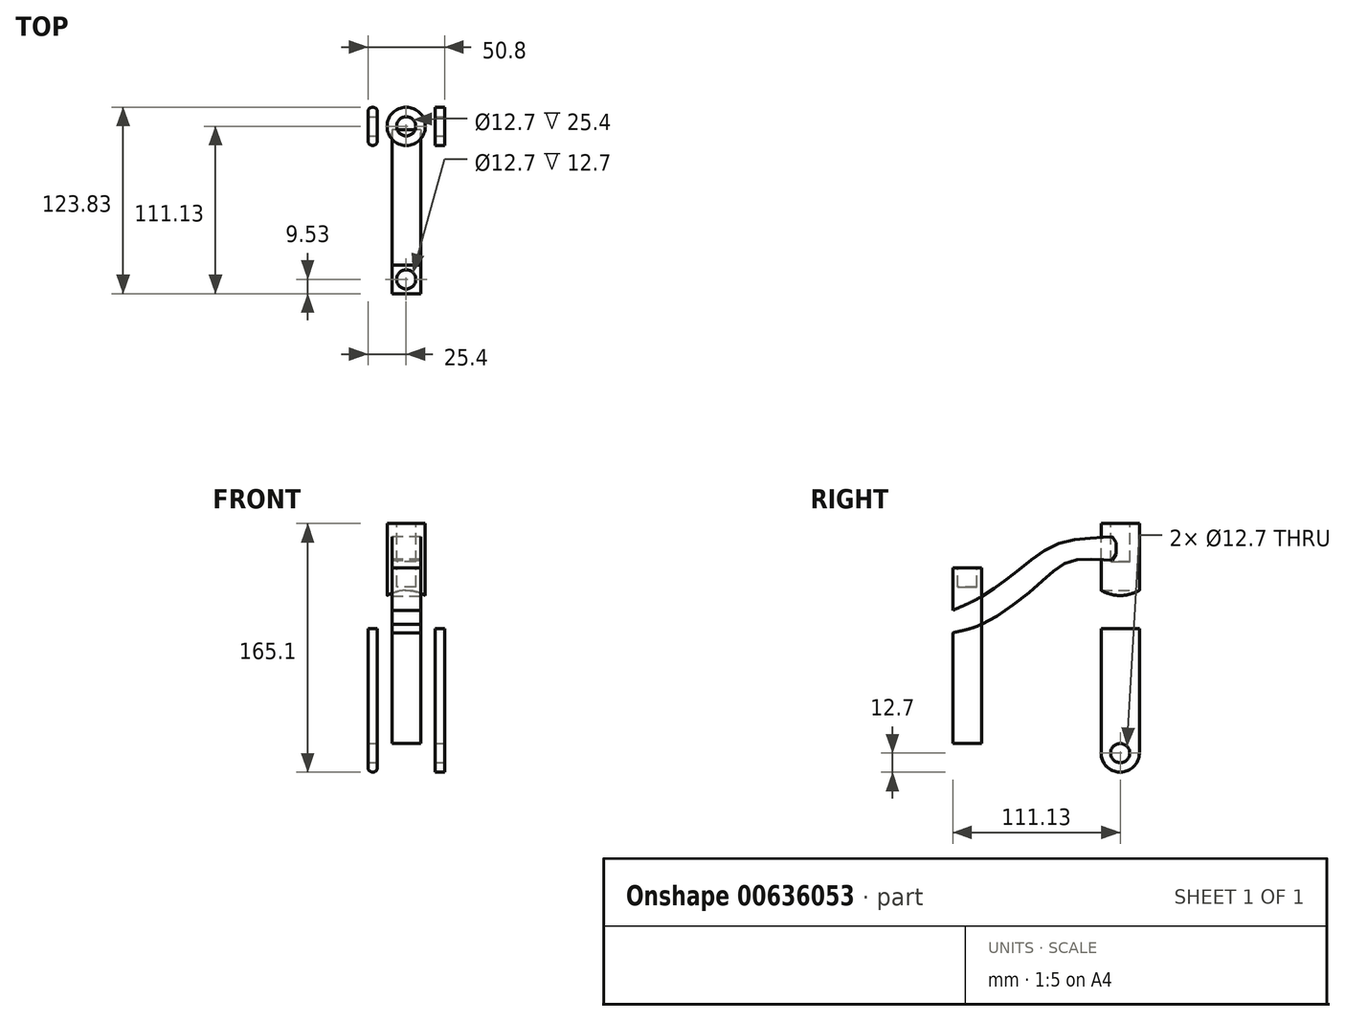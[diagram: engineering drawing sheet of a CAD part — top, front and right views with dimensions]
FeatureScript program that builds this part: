
annotation { "Feature Type Name" : "Feature", "Feature Type Description" : "" }
export const myFeature = defineFeature(function(context is Context, id is Id, definition is map)
    precondition{}
    {
        {
            var Q0;
            Q0=qCreatedBy(makeId("Front.planeOp"),FACE);
            var sketch = newSketch(context, id + "F0", { "sketchPlane" : qUnion([Q0])});
            skLineSegment(sketch, "E0", {"start": v(-133.38, 0) * mm, "end": v(142.58, 0) * mm});
            skLineSegment(sketch, "E1.0", {"start": v(-133.38, 12.7) * mm, "end": v(142.58, 12.7) * mm});
            skLineSegment(sketch, "E2.0", {"start": v(-133.38, 19.05) * mm, "end": v(142.58, 19.05) * mm});
            skLineSegment(sketch, "E3.0", {"start": v(-133.38, 88.9) * mm, "end": v(142.58, 88.9) * mm});
            skLineSegment(sketch, "E4", {"start": v(0, 134.77) * mm, "end": v(0, -117.55) * mm});
            skLineSegment(sketch, "E5.0", {"start": v(-19.05, 76.2) * mm, "end": v(-19.05, -19.05) * mm});
            skLineSegment(sketch, "E6.0", {"start": v(19.05, 76.2) * mm, "end": v(19.05, -19.05) * mm});
            skLineSegment(sketch, "E7.0", {"start": v(-133.38, 76.2) * mm, "end": v(142.58, 76.2) * mm});
            skArc(sketch, "E8", {"start": v(19.05, 76.2) * mm, "mid": v(0, 95.25) * mm, "end": v(-19.05, 76.2) * mm});
            skLineSegment(sketch, "E9.0", {"start": v(-6.35, 146.05) * mm, "end": v(-6.35, 100.8) * mm});
            skLineSegment(sketch, "E10.0", {"start": v(6.35, 146.05) * mm, "end": v(6.35, 100.8) * mm});
            skLineSegment(sketch, "E11.0", {"start": v(-12.7, 146.05) * mm, "end": v(12.7, 146.05) * mm});
            skLineSegment(sketch, "E12.0", {"start": v(-12.7, 146.05) * mm, "end": v(-12.7, 98.2) * mm});
            skLineSegment(sketch, "E12.2", {"start": v(12.7, 146.05) * mm, "end": v(12.7, 98.2) * mm});
            skLineSegment(sketch, "E13.0", {"start": v(25.4, 76.2) * mm, "end": v(25.4, -19.05) * mm});
            skArc(sketch, "E13.1", {"start": v(25.4, 76.2) * mm, "mid": v(0, 101.6) * mm, "end": v(-25.4, 76.2) * mm});
            skLineSegment(sketch, "E13.2", {"start": v(-25.4, 76.2) * mm, "end": v(-25.4, -19.05) * mm});
            skLineSegment(sketch, "E14.0", {"start": v(-25.4, -19.05) * mm, "end": v(-19.05, -19.05) * mm});
            skLineSegment(sketch, "E15.trimOffspring", {"start": v(19.05, -19.05) * mm, "end": v(25.4, -19.05) * mm});
            skLineSegment(sketch, "E16.trimOffspring", {"start": v(6.35, 94.16) * mm, "end": v(6.35, -117.55) * mm});
            skLineSegment(sketch, "E17.trimOffspring", {"start": v(-6.35, 94.16) * mm, "end": v(-6.35, -117.55) * mm});
            skSolve(sketch);
        }
        {
            var Q0;
            {var subQ4=sQuery(id+"F0.wireOp",EDGE,"E13.1");var subQ6=sQuery(id+"F0.wireOp",EDGE,"E3.0");var subQ8=makeQuery(id+"F0.imprint","INTERSECT",VERTEX,{"disambiguationData":[OD(0.0)],"derivedFrom":[subQ6,subQ4]});Q0=makeQuery(id+"F0.imprint","IMPRINT",FACE,{"disambiguationData":[TD([[makeQuery(id+"F0.imprint","IMPRINT",EDGE,{"disambiguationData":[TD([[subQ8,-1.0]])],"derivedFrom":subQ6}),1.0]])]});}
            var Q1;
            {var subQ0=sQuery(id+"F0.wireOp",EDGE,"E13.1");var subQ1=sQuery(id+"F0.wireOp",EDGE,"E3.0");var subQ2=makeQuery(id+"F0.imprint","INTERSECT",VERTEX,{"disambiguationData":[OD(0.0)],"derivedFrom":[subQ1,subQ0]});Q1=makeQuery(id+"F0.imprint","IMPRINT",FACE,{"disambiguationData":[TD([[makeQuery(id+"F0.imprint","IMPRINT",EDGE,{"disambiguationData":[TD([[subQ2,-1.0]])],"derivedFrom":subQ1}),-1.0]])]});}
            var Q2;
            {var subQ4=sQuery(id+"F0.wireOp",EDGE,"E13.1");var subQ6=sQuery(id+"F0.wireOp",EDGE,"E3.0");var subQ8=makeQuery(id+"F0.imprint","INTERSECT",VERTEX,{"disambiguationData":[OD(1.0)],"derivedFrom":[subQ6,subQ4]});Q2=makeQuery(id+"F0.imprint","IMPRINT",FACE,{"disambiguationData":[TD([[makeQuery(id+"F0.imprint","IMPRINT",EDGE,{"disambiguationData":[TD([[subQ8,1.0]])],"derivedFrom":subQ6}),1.0]])]});}
            var Q3;
            {var subQ0=sQuery(id+"F0.wireOp",EDGE,"E13.1");var subQ1=sQuery(id+"F0.wireOp",EDGE,"E3.0");var subQ2=makeQuery(id+"F0.imprint","INTERSECT",VERTEX,{"disambiguationData":[OD(1.0)],"derivedFrom":[subQ1,subQ0]});Q3=makeQuery(id+"F0.imprint","IMPRINT",FACE,{"disambiguationData":[TD([[makeQuery(id+"F0.imprint","IMPRINT",EDGE,{"disambiguationData":[TD([[subQ2,1.0]])],"derivedFrom":subQ1}),-1.0]])]});}
            var Q4;
            {var subQ0=sQuery(id+"F0.wireOp",EDGE,"E13.0");var subQ1=sQuery(id+"F0.wireOp",EDGE,"E2.0");var subQ2=makeQuery(id+"F0.imprint","INTERSECT",VERTEX,{"derivedFrom":[subQ1,subQ0]});Q4=makeQuery(id+"F0.imprint","IMPRINT",FACE,{"disambiguationData":[TD([[makeQuery(id+"F0.imprint","IMPRINT",EDGE,{"disambiguationData":[TD([[subQ2,1.0]])],"derivedFrom":subQ1}),1.0]])]});}
            var Q5;
            {var subQ0=sQuery(id+"F0.wireOp",EDGE,"E13.0");var subQ1=sQuery(id+"F0.wireOp",EDGE,"E1.0");var subQ2=makeQuery(id+"F0.imprint","INTERSECT",VERTEX,{"derivedFrom":[subQ1,subQ0]});Q5=makeQuery(id+"F0.imprint","IMPRINT",FACE,{"disambiguationData":[TD([[makeQuery(id+"F0.imprint","IMPRINT",EDGE,{"disambiguationData":[TD([[subQ2,1.0]])],"derivedFrom":subQ1}),1.0]])]});}
            var Q6;
            {var subQ0=sQuery(id+"F0.wireOp",EDGE,"E13.0");var subQ1=sQuery(id+"F0.wireOp",EDGE,"E0");var subQ2=makeQuery(id+"F0.imprint","INTERSECT",VERTEX,{"derivedFrom":[subQ1,subQ0]});Q6=makeQuery(id+"F0.imprint","IMPRINT",FACE,{"disambiguationData":[TD([[makeQuery(id+"F0.imprint","IMPRINT",EDGE,{"disambiguationData":[TD([[subQ2,1.0]])],"derivedFrom":subQ1}),1.0]])]});}
            var Q7;
            {var subQ5=sQuery(id+"F0.wireOp",EDGE,"E15.trimOffspring");Q7=makeQuery(id+"F0.imprint","IMPRINT",FACE,{"disambiguationData":[TD([[makeQuery(id+"F0.imprint","IMPRINT",EDGE,{"derivedFrom":subQ5}),1.0]])]});}
            var Q8;
            {var subQ5=sQuery(id+"F0.wireOp",EDGE,"E14.0");Q8=makeQuery(id+"F0.imprint","IMPRINT",FACE,{"disambiguationData":[TD([[makeQuery(id+"F0.imprint","IMPRINT",EDGE,{"derivedFrom":subQ5}),1.0]])]});}
            var Q9;
            {var subQ0=sQuery(id+"F0.wireOp",EDGE,"E13.2");var subQ1=sQuery(id+"F0.wireOp",EDGE,"E0");var subQ2=makeQuery(id+"F0.imprint","INTERSECT",VERTEX,{"derivedFrom":[subQ1,subQ0]});Q9=makeQuery(id+"F0.imprint","IMPRINT",FACE,{"disambiguationData":[TD([[makeQuery(id+"F0.imprint","IMPRINT",EDGE,{"disambiguationData":[TD([[subQ2,-1.0]])],"derivedFrom":subQ1}),1.0]])]});}
            var Q10;
            {var subQ0=sQuery(id+"F0.wireOp",EDGE,"E13.2");var subQ1=sQuery(id+"F0.wireOp",EDGE,"E1.0");var subQ2=makeQuery(id+"F0.imprint","INTERSECT",VERTEX,{"derivedFrom":[subQ1,subQ0]});Q10=makeQuery(id+"F0.imprint","IMPRINT",FACE,{"disambiguationData":[TD([[makeQuery(id+"F0.imprint","IMPRINT",EDGE,{"disambiguationData":[TD([[subQ2,-1.0]])],"derivedFrom":subQ1}),1.0]])]});}
            var Q11;
            {var subQ0=sQuery(id+"F0.wireOp",EDGE,"E13.2");var subQ1=sQuery(id+"F0.wireOp",EDGE,"E2.0");var subQ2=makeQuery(id+"F0.imprint","INTERSECT",VERTEX,{"derivedFrom":[subQ1,subQ0]});Q11=makeQuery(id+"F0.imprint","IMPRINT",FACE,{"disambiguationData":[TD([[makeQuery(id+"F0.imprint","IMPRINT",EDGE,{"disambiguationData":[TD([[subQ2,-1.0]])],"derivedFrom":subQ1}),1.0]])]});}
            extrude(context, id + "F1", {"entities" : qUnion([Q0, Q1, Q2, Q3, Q4, Q5, Q6, Q7, Q8, Q9, Q10, Q11]), "endBound" : BoundingType.SYMMETRIC, "oppositeDirection" : true, "depth" : 25.4 * mm, "offsetDistance" : 25.4 * mm});
        }
        {
            var Q0;
            Q0=makeQuery(id+"F1.opExtrude","CAP_EDGE",EDGE,{"disambiguationData":[OSD([sQuery(id+"F0.wireOp",EDGE,"E14.0")])],"isStart":true});
            var Q1;
            Q1=makeQuery(id+"F1.opExtrude","CAP_EDGE",EDGE,{"disambiguationData":[OSD([sQuery(id+"F0.wireOp",EDGE,"E15.trimOffspring")])],"isStart":true});
            var Q2;
            Q2=makeQuery(id+"F1.opExtrude","CAP_EDGE",EDGE,{"disambiguationData":[OSD([sQuery(id+"F0.wireOp",EDGE,"E15.trimOffspring")])],"isStart":false});
            var Q3;
            Q3=makeQuery(id+"F1.opExtrude","CAP_EDGE",EDGE,{"disambiguationData":[OSD([sQuery(id+"F0.wireOp",EDGE,"E14.0")])],"isStart":false});
            fillet(context, id + "F2", {"entities" : qUnion([Q0, Q1, Q2, Q3]), "radius" : 12.7 * mm, "tangentPropagation" : true, "allowEdgeOverflow" : false});
        }
        {
            var Q0;
            Q0=makeQuery(id+"F1.opExtrude","SWEPT_FACE",FACE,{"disambiguationData":[OSD([sQuery(id+"F0.wireOp",EDGE,"E13.2")])]});
            var sketch = newSketch(context, id + "F3", { "sketchPlane" : qUnion([Q0])});
            skCircle(sketch, "E18", {"center": v(0, -6.35) * mm, "radius": 6.35 * mm});
            skSolve(sketch);
        }
        {
            var Q0;
            Q0=makeQuery(id+"F3.imprint","IMPRINT",FACE,{"disambiguationData":[TD([[makeQuery(id+"F3.imprint","IMPRINT",EDGE,{"derivedFrom":sQuery(id+"F3.wireOp",EDGE,"E18")}),1.0]])]});
            var Q1;
            Q1=makeQuery(id+"F1.opExtrude","SWEPT_FACE",FACE,{"disambiguationData":[OSD([sQuery(id+"F0.wireOp",EDGE,"E13.0")])]});
            extrude(context, id + "F4", {"entities" : qUnion([Q0]), "operationType" : NewBodyOperationType.REMOVE, "depth" : 25.4 * mm, "offsetDistance" : 25.4 * mm, "hasSecondDirection" : true, "secondDirectionBound" : SecondDirectionBoundingType.UP_TO_SURFACE, "secondDirectionOppositeDirection" : true, "secondDirectionDepth" : 25.4 * mm, "secondDirectionBoundEntityFace" : qUnion([Q1])});
        }
        {
            var Q0;
            {var subQ0=sQuery(id+"F0.wireOp",EDGE,"E9.0");Q0=makeQuery(id+"F0.imprint","IMPRINT",FACE,{"disambiguationData":[TD([[makeQuery(id+"F0.imprint","IMPRINT",EDGE,{"derivedFrom":subQ0}),-1.0]])]});}
            var Q1;
            {var subQ4=sQuery(id+"F0.wireOp",EDGE,"E9.0");Q1=makeQuery(id+"F0.imprint","IMPRINT",FACE,{"disambiguationData":[TD([[makeQuery(id+"F0.imprint","IMPRINT",EDGE,{"derivedFrom":subQ4}),1.0]])]});}
            var Q2;
            {var subQ0=sQuery(id+"F0.wireOp",EDGE,"E10.0");Q2=makeQuery(id+"F0.imprint","IMPRINT",FACE,{"disambiguationData":[TD([[makeQuery(id+"F0.imprint","IMPRINT",EDGE,{"derivedFrom":subQ0}),1.0]])]});}
            extrude(context, id + "F5", {"entities" : qUnion([Q0, Q1, Q2]), "endBound" : BoundingType.SYMMETRIC, "depth" : 25.4 * mm, "offsetDistance" : 25.4 * mm});
        }
        {
            var Q0;
            Q0=makeQuery(id+"F5.opExtrude","SWEPT_FACE",FACE,{"disambiguationData":[OSD([sQuery(id+"F0.wireOp",EDGE,"E11.0")])]});
            var sketch = newSketch(context, id + "F6", { "sketchPlane" : qUnion([Q0])});
            skCircle(sketch, "E19", {"center": v(0, 0) * mm, "radius": 6.35 * mm});
            skSolve(sketch);
        }
        {
            var Q0;
            Q0=makeQuery(id+"F6.imprint","IMPRINT",FACE,{"disambiguationData":[TD([[makeQuery(id+"F6.imprint","IMPRINT",EDGE,{"derivedFrom":sQuery(id+"F6.wireOp",EDGE,"E19")}),1.0]])]});
            extrude(context, id + "F7", {"entities" : qUnion([Q0]), "operationType" : NewBodyOperationType.REMOVE, "oppositeDirection" : true, "depth" : 25.4 * mm, "offsetDistance" : 25.4 * mm});
        }
        {
            var Q0;
            Q0=makeQuery(id+"F5.opExtrude","CAP_EDGE",EDGE,{"disambiguationData":[OSD([sQuery(id+"F0.wireOp",EDGE,"E12.0")])],"isStart":true});
            var Q1;
            Q1=makeQuery(id+"F5.opExtrude","CAP_EDGE",EDGE,{"disambiguationData":[OSD([sQuery(id+"F0.wireOp",EDGE,"E12.0")])],"isStart":false});
            var Q2;
            Q2=makeQuery(id+"F5.opExtrude","CAP_EDGE",EDGE,{"disambiguationData":[OSD([sQuery(id+"F0.wireOp",EDGE,"E12.2")])],"isStart":false});
            var Q3;
            Q3=makeQuery(id+"F5.opExtrude","CAP_EDGE",EDGE,{"disambiguationData":[OSD([sQuery(id+"F0.wireOp",EDGE,"E12.2")])],"isStart":true});
            fillet(context, id + "F8", {"entities" : qUnion([Q0, Q1, Q2, Q3]), "radius" : 12.7 * mm, "tangentPropagation" : true, "allowEdgeOverflow" : false});
        }
        {
            var Q0;
            Q0=makeQuery(id+"F1.opExtrude","CAP_EDGE",EDGE,{"disambiguationData":[OSD([sQuery(id+"F0.wireOp",EDGE,"E13.2")])],"isStart":true});
            var Q1;
            Q1=makeQuery(id+"F1.opExtrude","CAP_EDGE",EDGE,{"disambiguationData":[OSD([sQuery(id+"F0.wireOp",EDGE,"E5.0")])],"isStart":true});
            fillet(context, id + "F9", {"entities" : qUnion([Q0, Q1]), "radius" : 3.17 * mm, "tangentPropagation" : true, "allowEdgeOverflow" : false});
        }
        {
            var Q0;
            Q0=qCreatedBy(makeId("Right.planeOp"),FACE);
            var sketch = newSketch(context, id + "F10", { "sketchPlane" : qUnion([Q0])});
            skLineSegment(sketch, "E20", {"start": v(0, 167.43) * mm, "end": v(0, -72.36) * mm});
            skLineSegment(sketch, "E21.0", {"start": v(-101.6, 167.43) * mm, "end": v(-101.6, -72.36) * mm});
            skLineSegment(sketch, "E22.0", {"start": v(-203.2, 167.43) * mm, "end": v(-203.2, 97.58) * mm});
            skLineSegment(sketch, "E23", {"start": v(-101.6, 167.43) * mm, "end": v(-203.2, 167.43) * mm});
            skLineSegment(sketch, "E24.0", {"start": v(-92.08, 116.63) * mm, "end": v(-111.13, 116.63) * mm});
            skLineSegment(sketch, "E25.0", {"start": v(-92.07, 97.58) * mm, "end": v(-111.12, 97.58) * mm});
            skLineSegment(sketch, "E26", {"start": v(0, 0) * mm, "end": v(-203.2, 0) * mm});
            skLineSegment(sketch, "E27.0", {"start": v(0, -12.7) * mm, "end": v(-203.2, -12.7) * mm});
            skLineSegment(sketch, "E28.0", {"start": v(0, -19.05) * mm, "end": v(-203.2, -19.05) * mm});
            skCircle(sketch, "E29", {"center": v(-203.2, -6.35) * mm, "radius": 6.35 * mm});
            skCircle(sketch, "E30", {"center": v(-203.2, -6.35) * mm, "radius": 12.7 * mm});
            skLineSegment(sketch, "E31.0", {"start": v(-92.08, 116.63) * mm, "end": v(-92.07, -72.36) * mm});
            skLineSegment(sketch, "E32.0", {"start": v(-111.13, 116.63) * mm, "end": v(-111.12, -72.36) * mm});
            skFitSpline(sketch, "E33", {"points": [v(-10.52, 136.84) * mm, v(-39.13, 133.26) * mm, v(-67.1, 115.5) * mm, v(-92.07, 97.58) * mm, v(-118.86, 85.47) * mm, v(-159.5, 64.15) * mm, v(-211.86, 2.93) * mm, v(-211.9, -2.96) * mm, v(-194.22, -10.04) * mm, v(-190.5, -6.35) * mm, v(-186.18, 10.6) * mm, v(-156.28, 51.58) * mm, v(-116.42, 72.26) * mm, v(-92.07, 79.05) * mm, v(-53.74, 105.85) * mm, v(-33.35, 120.81) * mm, v(-10.16, 121.75) * mm, v(-3.8, 122.9) * mm, v(-3.57, 135.9) * mm, v(-10.52, 136.84) * mm]});
            skSolve(sketch);
        }
        {
            var Q0;
            {var subQ0=sQuery(id+"F10.wireOp",EDGE,"E33");var subQ1=sQuery(id+"F10.wireOp",EDGE,"E31.0");var subQ3=makeQuery(id+"F10.imprint","INTERSECT",VERTEX,{"derivedFrom":[subQ1,subQ0]});Q0=makeQuery(id+"F10.imprint","IMPRINT",FACE,{"disambiguationData":[TD([[makeQuery(id+"F10.imprint","IMPRINT",EDGE,{"disambiguationData":[TD([[subQ3,1.0]])],"derivedFrom":subQ1}),1.0]])]});}
            extrude(context, id + "F11", {"entities" : qUnion([Q0]), "endBound" : BoundingType.SYMMETRIC, "depth" : 19.05 * mm, "offsetDistance" : 25.4 * mm});
        }
        {
            var Q0;
            {var subQ0=sQuery(id+"F10.wireOp",EDGE,"E24.0");var subQ1=sQuery(id+"F10.wireOp",EDGE,"E21.0");var subQ2=makeQuery(id+"F10.imprint","INTERSECT",VERTEX,{"derivedFrom":[subQ1,subQ0]});Q0=makeQuery(id+"F10.imprint","IMPRINT",FACE,{"disambiguationData":[TD([[makeQuery(id+"F10.imprint","IMPRINT",EDGE,{"disambiguationData":[TD([[subQ2,-1.0]])],"derivedFrom":subQ1}),-1.0]])]});}
            var Q1;
            {var subQ0=sQuery(id+"F10.wireOp",EDGE,"E24.0");var subQ1=sQuery(id+"F10.wireOp",EDGE,"E21.0");var subQ2=makeQuery(id+"F10.imprint","INTERSECT",VERTEX,{"derivedFrom":[subQ1,subQ0]});Q1=makeQuery(id+"F10.imprint","IMPRINT",FACE,{"disambiguationData":[TD([[makeQuery(id+"F10.imprint","IMPRINT",EDGE,{"disambiguationData":[TD([[subQ2,-1.0]])],"derivedFrom":subQ1}),1.0]])]});}
            var Q2;
            {var subQ0=sQuery(id+"F10.wireOp",EDGE,"E25.0");var subQ1=sQuery(id+"F10.wireOp",EDGE,"E21.0");var subQ2=makeQuery(id+"F10.imprint","INTERSECT",VERTEX,{"derivedFrom":[subQ1,subQ0]});Q2=makeQuery(id+"F10.imprint","IMPRINT",FACE,{"disambiguationData":[TD([[makeQuery(id+"F10.imprint","IMPRINT",EDGE,{"disambiguationData":[TD([[subQ2,-1.0]])],"derivedFrom":subQ1}),-1.0]])]});}
            var Q3;
            {var subQ0=sQuery(id+"F10.wireOp",EDGE,"E25.0");var subQ1=sQuery(id+"F10.wireOp",EDGE,"E21.0");var subQ2=makeQuery(id+"F10.imprint","INTERSECT",VERTEX,{"derivedFrom":[subQ1,subQ0]});Q3=makeQuery(id+"F10.imprint","IMPRINT",FACE,{"disambiguationData":[TD([[makeQuery(id+"F10.imprint","IMPRINT",EDGE,{"disambiguationData":[TD([[subQ2,-1.0]])],"derivedFrom":subQ1}),1.0]])]});}
            var Q4;
            {var subQ0=sQuery(id+"F10.wireOp",EDGE,"E33");var subQ1=sQuery(id+"F10.wireOp",EDGE,"E21.0");var subQ2=makeQuery(id+"F10.imprint","INTERSECT",VERTEX,{"disambiguationData":[OD(0.0)],"derivedFrom":[subQ1,subQ0]});Q4=makeQuery(id+"F10.imprint","IMPRINT",FACE,{"disambiguationData":[TD([[makeQuery(id+"F10.imprint","IMPRINT",EDGE,{"disambiguationData":[TD([[subQ2,-1.0]])],"derivedFrom":subQ1}),1.0]])]});}
            var Q5;
            {var subQ0=sQuery(id+"F10.wireOp",EDGE,"E33");var subQ1=sQuery(id+"F10.wireOp",EDGE,"E21.0");var subQ2=makeQuery(id+"F10.imprint","INTERSECT",VERTEX,{"disambiguationData":[OD(0.0)],"derivedFrom":[subQ1,subQ0]});Q5=makeQuery(id+"F10.imprint","IMPRINT",FACE,{"disambiguationData":[TD([[makeQuery(id+"F10.imprint","IMPRINT",EDGE,{"disambiguationData":[TD([[subQ2,-1.0]])],"derivedFrom":subQ1}),-1.0]])]});}
            extrude(context, id + "F12", {"entities" : qUnion([Q0, Q1, Q2, Q3, Q4, Q5]), "endBound" : BoundingType.SYMMETRIC, "depth" : 19.05 * mm, "offsetDistance" : 25.4 * mm});
        }
        {
            var Q0;
            Q0=makeQuery(id+"F12.opExtrude","SWEPT_FACE",FACE,{"disambiguationData":[OSD([sQuery(id+"F10.wireOp",EDGE,"E24.0")])]});
            var sketch = newSketch(context, id + "F13", { "sketchPlane" : qUnion([Q0])});
            skCircle(sketch, "E34", {"center": v(0, -101.6) * mm, "radius": 6.35 * mm});
            skSolve(sketch);
        }
        {
            var Q0;
            Q0=makeQuery(id+"F13.imprint","IMPRINT",FACE,{"disambiguationData":[TD([[makeQuery(id+"F13.imprint","IMPRINT",EDGE,{"derivedFrom":sQuery(id+"F13.wireOp",EDGE,"E34")}),1.0]])]});
            extrude(context, id + "F14", {"entities" : qUnion([Q0]), "operationType" : NewBodyOperationType.REMOVE, "oppositeDirection" : true, "depth" : 12.7 * mm, "offsetDistance" : 25.4 * mm});
        }
    });
